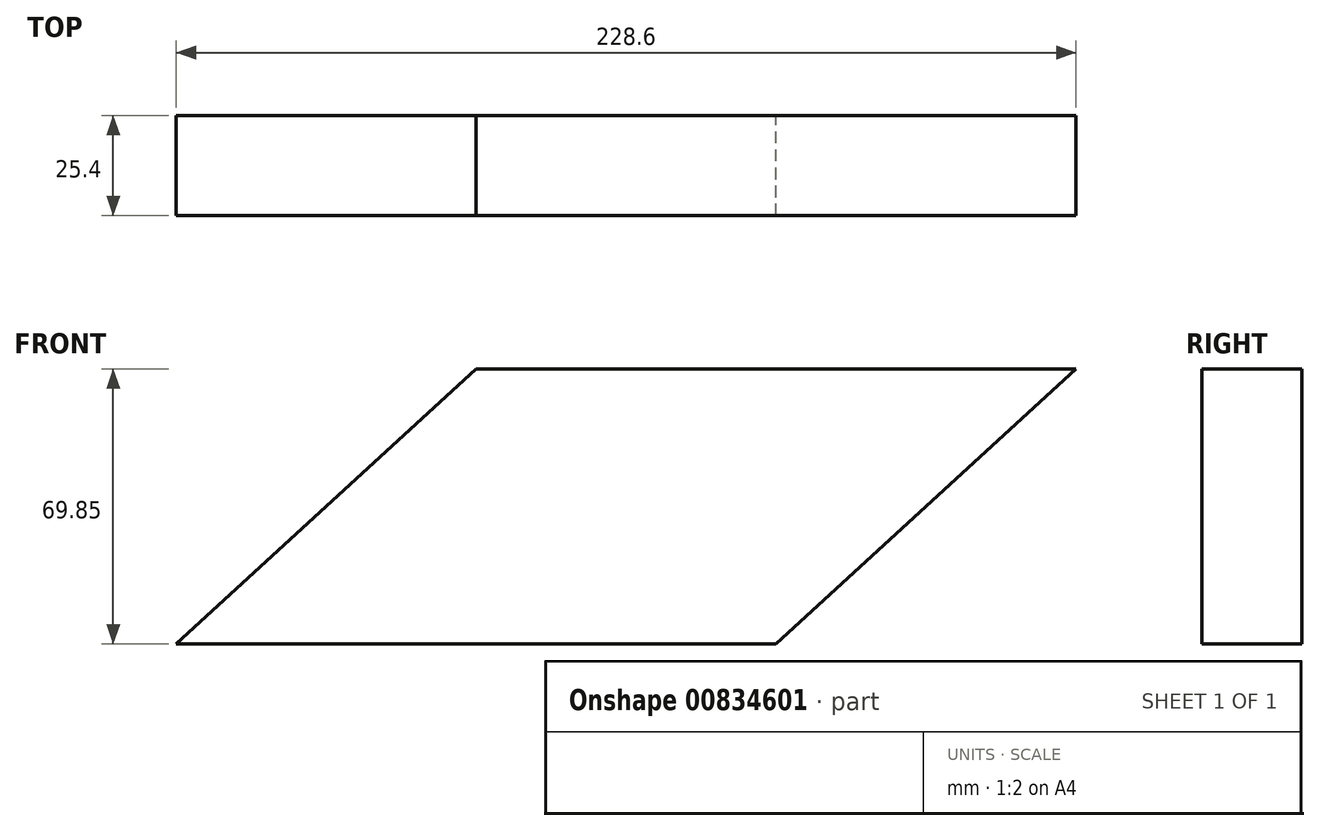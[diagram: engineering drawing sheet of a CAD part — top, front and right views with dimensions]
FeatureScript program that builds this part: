
annotation { "Feature Type Name" : "Feature", "Feature Type Description" : "" }
export const myFeature = defineFeature(function(context is Context, id is Id, definition is map)
    precondition{}
    {
        {
            var Q0;
            Q0=qCreatedBy(makeId("Front.planeOp"),FACE);
            var sketch = newSketch(context, id + "F0", { "sketchPlane" : qUnion([Q0])});
            skLineSegment(sketch, "E0", {"start": v(0, 0) * mm, "end": v(152.4, 0) * mm});
            skLineSegment(sketch, "E1", {"start": v(152.4, 0) * mm, "end": v(228.6, 69.85) * mm});
            skLineSegment(sketch, "E2", {"start": v(228.6, 69.85) * mm, "end": v(76.2, 69.85) * mm});
            skLineSegment(sketch, "E3", {"start": v(76.2, 69.85) * mm, "end": v(0, 0) * mm});
            skSolve(sketch);
        }
        {
            var Q0;
            Q0 = qSketchRegion(id + "F0", true);
            extrude(context, id + "F1", {"entities" : qUnion([Q0]), "depth" : 25.4 * mm, "offsetDistance" : 25.4 * mm});
        }
    });
